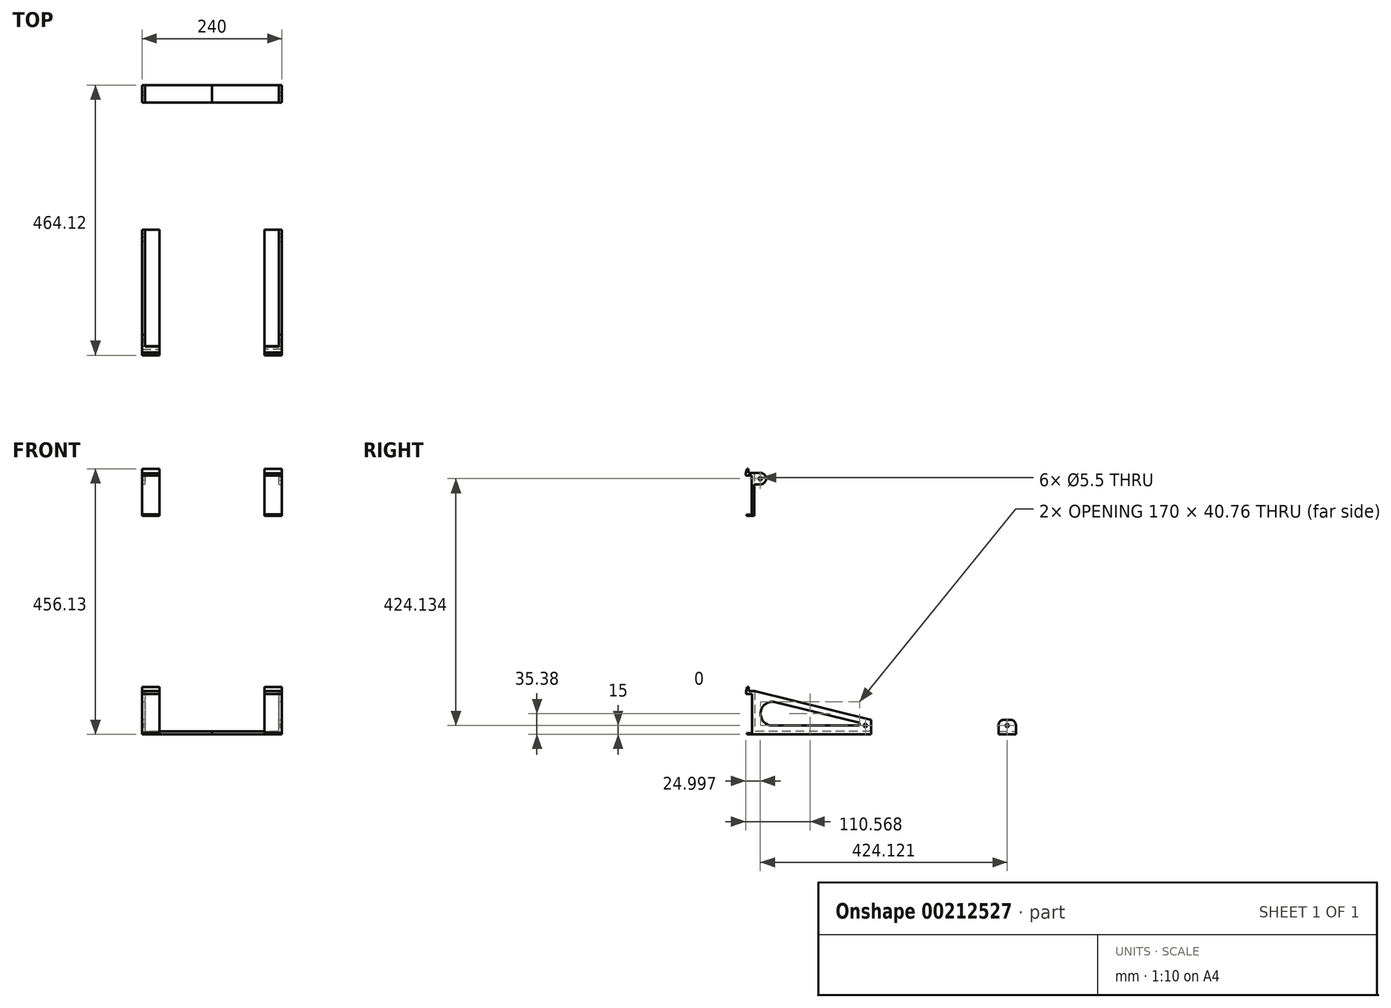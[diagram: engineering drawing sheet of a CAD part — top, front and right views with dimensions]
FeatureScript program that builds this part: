
annotation { "Feature Type Name" : "Feature", "Feature Type Description" : "" }
export const myFeature = defineFeature(function(context is Context, id is Id, definition is map)
    precondition{}
    {
        {
            var Q0;
            Q0=qCreatedBy(makeId("Right.planeOp"),FACE);
            var sketch = newSketch(context, id + "F0", { "sketchPlane" : qUnion([Q0])});
            skLineSegment(sketch, "E0", {"start": v(2.67, -35.24) * mm, "end": v(2.67, 31.76) * mm});
            skLineSegment(sketch, "E1", {"start": v(2.67, 31.76) * mm, "end": v(-7.33, 31.76) * mm});
            skLineSegment(sketch, "E2", {"start": v(-7.33, 31.76) * mm, "end": v(-7.33, 36.87) * mm});
            skLineSegment(sketch, "E3", {"start": v(-5.08, 43.76) * mm, "end": v(-2.83, 43.76) * mm});
            skLineSegment(sketch, "E4", {"start": v(-2.83, 43.76) * mm, "end": v(-2.83, 36.76) * mm});
            skLineSegment(sketch, "E5", {"start": v(-2.83, 36.76) * mm, "end": v(7.67, 36.76) * mm});
            skLineSegment(sketch, "E6", {"start": v(7.67, 36.76) * mm, "end": v(7.67, -32.24) * mm});
            skLineSegment(sketch, "E7", {"start": v(7.67, -37.24) * mm, "end": v(-5.83, -37.24) * mm});
            skLineSegment(sketch, "E8", {"start": v(-5.83, -37.24) * mm, "end": v(-5.83, -35.24) * mm});
            skLineSegment(sketch, "E9", {"start": v(-2.83, -35.24) * mm, "end": v(2.67, -35.24) * mm});
            skLineSegment(sketch, "E10", {"start": v(-5.08, 43.76) * mm, "end": v(-7.33, 36.87) * mm});
            skPoint(sketch, "E11.orphan", {"position": v(-7.33, 43.76) * mm});
            skLineSegment(sketch, "E12", {"start": v(-2.83, -35.24) * mm, "end": v(-4.33, -34.5) * mm});
            skLineSegment(sketch, "E13", {"start": v(-4.33, -34.5) * mm, "end": v(-5.83, -35.24) * mm});
            skPoint(sketch, "E14.orphan", {"position": v(-5.83, -34.5) * mm});
            skLineSegment(sketch, "E15", {"start": v(7.67, -37.24) * mm, "end": v(207.67, -37.24) * mm});
            skLineSegment(sketch, "E16", {"start": v(207.67, -37.24) * mm, "end": v(207.67, -32.24) * mm});
            skLineSegment(sketch, "E17", {"start": v(207.67, -32.24) * mm, "end": v(7.67, -32.24) * mm});
            skSolve(sketch);
        }
        {
            var Q0;
            Q0=makeQuery(id+"F0.imprint","IMPRINT",FACE,{"disambiguationData":[TD([[makeQuery(id+"F0.imprint","IMPRINT",EDGE,{"derivedFrom":sQuery(id+"F0.wireOp",EDGE,"E0")}),-1.0]])]});
            extrude(context, id + "F1", {"entities" : qUnion([Q0]), "depth" : 30 * mm});
        }
        {
            var Q0;
            Q0=makeQuery(id+"F1.opExtrude","CAP_FACE",FACE,{"disambiguationData":[OSD([sQuery(id+"F0.wireOp",EDGE,"E0"),sQuery(id+"F0.wireOp",EDGE,"E1"),sQuery(id+"F0.wireOp",EDGE,"E2"),sQuery(id+"F0.wireOp",EDGE,"E3"),sQuery(id+"F0.wireOp",EDGE,"E4"),sQuery(id+"F0.wireOp",EDGE,"E5"),sQuery(id+"F0.wireOp",EDGE,"E6"),sQuery(id+"F0.wireOp",EDGE,"E7"),sQuery(id+"F0.wireOp",EDGE,"E8"),sQuery(id+"F0.wireOp",EDGE,"E9"),sQuery(id+"F0.wireOp",EDGE,"E10"),sQuery(id+"F0.wireOp",EDGE,"E12"),sQuery(id+"F0.wireOp",EDGE,"E13"),sQuery(id+"F0.wireOp",EDGE,"E15"),sQuery(id+"F0.wireOp",EDGE,"E16"),sQuery(id+"F0.wireOp",EDGE,"E17")])],"isStart":false});
            var sketch = newSketch(context, id + "F2", { "sketchPlane" : qUnion([Q0])});
            skLineSegment(sketch, "E18", {"start": v(7.67, 36.76) * mm, "end": v(7.67, -32.24) * mm});
            skLineSegment(sketch, "E19", {"start": v(7.67, -32.24) * mm, "end": v(207.67, -32.24) * mm});
            skLineSegment(sketch, "E20", {"start": v(207.67, -32.24) * mm, "end": v(207.67, -12.24) * mm});
            skLineSegment(sketch, "E21", {"start": v(207.67, -12.24) * mm, "end": v(7.67, 36.76) * mm});
            skLineSegment(sketch, "E22", {"start": v(207.67, -22.24) * mm, "end": v(197.67, -22.24) * mm, "construction": true});
            skPoint(sketch, "E22.endSnap0", {"position": v(207.67, -22.24) * mm});
            skCircle(sketch, "E23", {"center": v(197.67, -22.24) * mm, "radius": 2.75 * mm});
            skLineSegment(sketch, "E24", {"start": v(207.67, -32.24) * mm, "end": v(187.67, -32.24) * mm, "construction": true});
            skLineSegment(sketch, "E25", {"start": v(187.67, -32.24) * mm, "end": v(187.67, -22.24) * mm, "construction": true});
            skLineSegment(sketch, "E26", {"start": v(187.67, -22.24) * mm, "end": v(17.67, -22.24) * mm});
            skLineSegment(sketch, "E27", {"start": v(187.67, -22.24) * mm, "end": v(187.67, -17.64) * mm});
            skLineSegment(sketch, "E28.trimOffspring", {"start": v(17.67, 24.01) * mm, "end": v(17.67, -22.24) * mm});
            skLineSegment(sketch, "E29.trimOffspring", {"start": v(187.67, -17.64) * mm, "end": v(17.67, 24.01) * mm});
            skSolve(sketch);
        }
        {
            var Q0;
            Q0=makeQuery(id+"F2.imprint","IMPRINT",FACE,{"disambiguationData":[TD([[makeQuery(id+"F2.imprint","IMPRINT",EDGE,{"derivedFrom":sQuery(id+"F2.wireOp",EDGE,"E18")}),1.0]])]});
            extrude(context, id + "F3", {"entities" : qUnion([Q0]), "operationType" : NewBodyOperationType.ADD, "oppositeDirection" : true, "depth" : 5 * mm});
        }
        {
            var Q0;
            Q0=makeQuery(id+"F3.opExtrude","SWEPT_EDGE",EDGE,{"disambiguationData":[OSD([sQuery(id+"F2.wireOp",EDGE,"E26"),sQuery(id+"F2.wireOp",EDGE,"E28.trimOffspring")])]});
            var Q1;
            Q1=makeQuery(id+"F3.opExtrude","SWEPT_EDGE",EDGE,{"disambiguationData":[OSD([sQuery(id+"F2.wireOp",EDGE,"E28.trimOffspring"),sQuery(id+"F2.wireOp",EDGE,"E29.trimOffspring")])]});
            fillet(context, id + "F4", {"entities" : qUnion([Q0, Q1]), "radius" : 20 * mm, "tangentPropagation" : true, "allowEdgeOverflow" : false});
        }
        {
            var Q0;
            Q0=makeQuery(id+"F3.opExtrude","SWEPT_EDGE",EDGE,{"disambiguationData":[OSD([sQuery(id+"F2.wireOp",EDGE,"E26"),sQuery(id+"F2.wireOp",EDGE,"E27")])]});
            var Q1;
            Q1=makeQuery(id+"F3.opExtrude","SWEPT_EDGE",EDGE,{"disambiguationData":[OSD([sQuery(id+"F2.wireOp",EDGE,"E27"),sQuery(id+"F2.wireOp",EDGE,"E29.trimOffspring")])]});
            fillet(context, id + "F5", {"entities" : qUnion([Q0, Q1]), "radius" : 2 * mm, "tangentPropagation" : true, "allowEdgeOverflow" : false});
        }
        {
            var Q0;
            Q0=qCreatedBy(makeId("Right.planeOp"),FACE);
            var sketch = newSketch(context, id + "F6", { "sketchPlane" : qUnion([Q0])});
            skLineSegment(sketch, "E30", {"start": v(0, 0) * mm, "end": v(0, 375) * mm, "construction": true});
            skLineSegment(sketch, "E31", {"start": v(2.1, 339.9) * mm, "end": v(2.1, 406.9) * mm});
            skLineSegment(sketch, "E32", {"start": v(2.1, 406.9) * mm, "end": v(-7.9, 406.9) * mm});
            skLineSegment(sketch, "E33", {"start": v(-7.9, 406.9) * mm, "end": v(-7.9, 411.32) * mm});
            skLineSegment(sketch, "E34", {"start": v(-5.65, 418.9) * mm, "end": v(-3.4, 418.9) * mm});
            skLineSegment(sketch, "E35", {"start": v(-3.4, 418.9) * mm, "end": v(-3.4, 411.9) * mm});
            skLineSegment(sketch, "E36", {"start": v(-3.4, 411.9) * mm, "end": v(7.1, 411.9) * mm});
            skLineSegment(sketch, "E37", {"start": v(7.1, 411.9) * mm, "end": v(7.1, 337.9) * mm});
            skLineSegment(sketch, "E38", {"start": v(7.1, 337.9) * mm, "end": v(-6.4, 337.9) * mm});
            skLineSegment(sketch, "E39", {"start": v(-6.4, 337.9) * mm, "end": v(-6.4, 339.9) * mm});
            skLineSegment(sketch, "E40", {"start": v(-3.4, 339.9) * mm, "end": v(2.1, 339.9) * mm});
            skLineSegment(sketch, "E41", {"start": v(-5.65, 418.9) * mm, "end": v(-7.9, 411.32) * mm});
            skPoint(sketch, "E42.orphan", {"position": v(-7.9, 418.9) * mm});
            skLineSegment(sketch, "E43", {"start": v(-3.4, 339.9) * mm, "end": v(-4.9, 340.64) * mm});
            skLineSegment(sketch, "E44", {"start": v(-4.9, 340.64) * mm, "end": v(-6.4, 339.9) * mm});
            skSolve(sketch);
        }
        {
            var Q0;
            Q0=makeQuery(id+"F6.imprint","IMPRINT",FACE,{"disambiguationData":[TD([[makeQuery(id+"F6.imprint","IMPRINT",EDGE,{"derivedFrom":sQuery(id+"F6.wireOp",EDGE,"E31")}),-1.0]])]});
            extrude(context, id + "F7", {"entities" : qUnion([Q0]), "depth" : 30 * mm});
        }
        {
            var Q0;
            Q0=makeQuery(id+"F7.opExtrude","CAP_FACE",FACE,{"disambiguationData":[OSD([sQuery(id+"F6.wireOp",EDGE,"E31"),sQuery(id+"F6.wireOp",EDGE,"E32"),sQuery(id+"F6.wireOp",EDGE,"E33"),sQuery(id+"F6.wireOp",EDGE,"E34"),sQuery(id+"F6.wireOp",EDGE,"E35"),sQuery(id+"F6.wireOp",EDGE,"E36"),sQuery(id+"F6.wireOp",EDGE,"E37"),sQuery(id+"F6.wireOp",EDGE,"E38"),sQuery(id+"F6.wireOp",EDGE,"E39"),sQuery(id+"F6.wireOp",EDGE,"E40"),sQuery(id+"F6.wireOp",EDGE,"E41"),sQuery(id+"F6.wireOp",EDGE,"E43"),sQuery(id+"F6.wireOp",EDGE,"E44")])],"isStart":false});
            var sketch = newSketch(context, id + "F8", { "sketchPlane" : qUnion([Q0])});
            skLineSegment(sketch, "E45", {"start": v(7.1, 411.9) * mm, "end": v(27.1, 411.9) * mm});
            skLineSegment(sketch, "E46", {"start": v(27.1, 411.9) * mm, "end": v(27.1, 391.9) * mm});
            skLineSegment(sketch, "E47", {"start": v(27.1, 391.9) * mm, "end": v(7.1, 391.9) * mm});
            skLineSegment(sketch, "E48", {"start": v(7.1, 391.9) * mm, "end": v(7.1, 411.9) * mm});
            skLineSegment(sketch, "E49", {"start": v(27.1, 401.9) * mm, "end": v(17.1, 401.9) * mm, "construction": true});
            skCircle(sketch, "E50", {"center": v(17.1, 401.9) * mm, "radius": 2.75 * mm});
            skSolve(sketch);
        }
        {
            var Q0;
            Q0=makeQuery(id+"F8.imprint","IMPRINT",FACE,{"disambiguationData":[TD([[makeQuery(id+"F8.imprint","IMPRINT",EDGE,{"derivedFrom":sQuery(id+"F8.wireOp",EDGE,"E45")}),-1.0]])]});
            extrude(context, id + "F9", {"entities" : qUnion([Q0]), "operationType" : NewBodyOperationType.ADD, "oppositeDirection" : true, "depth" : 5 * mm});
        }
        {
            var Q0;
            Q0=makeQuery(id+"F9.opExtrude","SWEPT_EDGE",EDGE,{"disambiguationData":[OSD([sQuery(id+"F8.wireOp",EDGE,"E45"),sQuery(id+"F8.wireOp",EDGE,"E46")])]});
            var Q1;
            Q1=makeQuery(id+"F9.opExtrude","SWEPT_EDGE",EDGE,{"disambiguationData":[OSD([sQuery(id+"F8.wireOp",EDGE,"E46"),sQuery(id+"F8.wireOp",EDGE,"E47")])]});
            var Q2;
            Q2=makeQuery(id+"F9.opExtrude","SWEPT_EDGE",EDGE,{"disambiguationData":[OSD([sQuery(id+"F6.wireOp",EDGE,"E37"),sQuery(id+"F8.wireOp",EDGE,"E47"),sQuery(id+"F8.wireOp",EDGE,"E48")])]});
            fillet(context, id + "F10", {"entities" : qUnion([Q0, Q1, Q2]), "radius" : 10 * mm, "tangentPropagation" : true, "allowEdgeOverflow" : false});
        }
        {
            var Q0;
            Q0=makeQuery(id+"F9.boolean.opBoolean","MERGE",FACE,{"derivedFrom":[makeQuery(id+"F7.opExtrude","CAP_FACE",FACE,{"disambiguationData":[OSD([sQuery(id+"F6.wireOp",EDGE,"E31"),sQuery(id+"F6.wireOp",EDGE,"E32"),sQuery(id+"F6.wireOp",EDGE,"E33"),sQuery(id+"F6.wireOp",EDGE,"E34"),sQuery(id+"F6.wireOp",EDGE,"E35"),sQuery(id+"F6.wireOp",EDGE,"E36"),sQuery(id+"F6.wireOp",EDGE,"E37"),sQuery(id+"F6.wireOp",EDGE,"E38"),sQuery(id+"F6.wireOp",EDGE,"E39"),sQuery(id+"F6.wireOp",EDGE,"E40"),sQuery(id+"F6.wireOp",EDGE,"E41"),sQuery(id+"F6.wireOp",EDGE,"E43"),sQuery(id+"F6.wireOp",EDGE,"E44")])],"isStart":false}),makeQuery(id+"F9.opExtrude","CAP_FACE",FACE,{"disambiguationData":[OSD([sQuery(id+"F8.wireOp",EDGE,"E45"),sQuery(id+"F8.wireOp",EDGE,"E46"),sQuery(id+"F8.wireOp",EDGE,"E47"),sQuery(id+"F8.wireOp",EDGE,"E48"),sQuery(id+"F8.wireOp",EDGE,"E50")])],"isStart":true})]});
            var sketch = newSketch(context, id + "F11", { "sketchPlane" : qUnion([Q0])});
            skLineSegment(sketch, "E51", {"start": v(17.1, 401.9) * mm, "end": v(782.83, -363.84) * mm, "construction": true});
            skLineSegment(sketch, "E52", {"start": v(17.1, 401.9) * mm, "end": v(17.1, -201.82) * mm, "construction": true});
            skLineSegment(sketch, "E53", {"start": v(197.74, -22.23) * mm, "end": v(609.04, -22.23) * mm, "construction": true});
            skCircle(sketch, "E54", {"center": v(441.22, -22.23) * mm, "radius": 2.75 * mm});
            skLineSegment(sketch, "E55", {"start": v(441.22, -22.23) * mm, "end": v(441.22, -37.23) * mm, "construction": true});
            skLineSegment(sketch, "E56", {"start": v(441.22, -37.23) * mm, "end": v(426.22, -37.23) * mm});
            skLineSegment(sketch, "E57", {"start": v(426.22, -37.23) * mm, "end": v(426.22, -12.23) * mm});
            skLineSegment(sketch, "E58", {"start": v(426.22, -12.23) * mm, "end": v(456.22, -12.23) * mm});
            skLineSegment(sketch, "E59", {"start": v(456.22, -12.23) * mm, "end": v(456.22, -37.23) * mm});
            skLineSegment(sketch, "E60", {"start": v(456.22, -37.23) * mm, "end": v(441.22, -37.23) * mm});
            skSolve(sketch);
        }
        {
            var Q0;
            Q0=makeQuery(id+"F11.imprint","IMPRINT",FACE,{"disambiguationData":[TD([[makeQuery(id+"F11.imprint","IMPRINT",EDGE,{"derivedFrom":sQuery(id+"F11.wireOp",EDGE,"E54")}),-1.0]])]});
            extrude(context, id + "F12", {"entities" : qUnion([Q0]), "oppositeDirection" : true, "depth" : 5 * mm});
        }
        {
            var Q0;
            Q0=makeQuery(id+"F12.opExtrude","SWEPT_EDGE",EDGE,{"disambiguationData":[OSD([sQuery(id+"F11.wireOp",EDGE,"E57"),sQuery(id+"F11.wireOp",EDGE,"E58")])]});
            var Q1;
            Q1=makeQuery(id+"F12.opExtrude","SWEPT_EDGE",EDGE,{"disambiguationData":[OSD([sQuery(id+"F11.wireOp",EDGE,"E58"),sQuery(id+"F11.wireOp",EDGE,"E59")])]});
            fillet(context, id + "F13", {"entities" : qUnion([Q0, Q1]), "radius" : 10 * mm, "tangentPropagation" : true, "allowEdgeOverflow" : false});
        }
        {
            var Q0;
            Q0=makeQuery(id+"F12.opExtrude","SWEPT_FACE",FACE,{"disambiguationData":[OSD([sQuery(id+"F11.wireOp",EDGE,"E59")])]});
            var sketch = newSketch(context, id + "F14", { "sketchPlane" : qUnion([Q0])});
            skLineSegment(sketch, "E61", {"start": v(-25, -37.23) * mm, "end": v(90, -37.23) * mm});
            skLineSegment(sketch, "E62", {"start": v(90, -37.23) * mm, "end": v(90, -32.23) * mm});
            skLineSegment(sketch, "E63", {"start": v(90, -32.23) * mm, "end": v(-25, -32.23) * mm});
            skLineSegment(sketch, "E64", {"start": v(-25, -32.23) * mm, "end": v(-25, -37.23) * mm});
            skSolve(sketch);
        }
        {
            var Q0;
            Q0=makeQuery(id+"F14.imprint","IMPRINT",FACE,{"disambiguationData":[TD([[makeQuery(id+"F14.imprint","IMPRINT",EDGE,{"derivedFrom":sQuery(id+"F14.wireOp",EDGE,"E61")}),1.0]])]});
            extrude(context, id + "F15", {"entities" : qUnion([Q0]), "operationType" : NewBodyOperationType.ADD, "oppositeDirection" : true, "depth" : 30 * mm});
        }
        {
            var Q0;
            Q0=qCreatedBy(makeId("Right.planeOp"),FACE);
            cPlane(context, id + "F16", {"entities" : qUnion([Q0]), "cplaneType" : CPlaneType.OFFSET, "offset" : 90 * mm, "oppositeDirection" : true, "width" : 150 * mm, "height" : 150 * mm});
        }
        {
            var Q0;
            Q0=makeQuery(id+"F12.opExtrude","SWEPT_BODY",BODY,{"disambiguationData":[OSD([sQuery(id+"F11.wireOp",EDGE,"E54"),sQuery(id+"F11.wireOp",EDGE,"E56"),sQuery(id+"F11.wireOp",EDGE,"E57"),sQuery(id+"F11.wireOp",EDGE,"E58"),sQuery(id+"F11.wireOp",EDGE,"E59"),sQuery(id+"F11.wireOp",EDGE,"E60")])]});
            var Q1;
            Q1=qCreatedBy(id+"F16.planeOp",FACE);
            mirror(context, id + "F17", {"operationType" : NewBodyOperationType.ADD, "entities" : qUnion([Q0]), "mirrorPlane" : qUnion([Q1])});
        }
        {
            var Q0;
            Q0=makeQuery(id+"F1.opExtrude","SWEPT_BODY",BODY,{"disambiguationData":[OSD([sQuery(id+"F0.wireOp",EDGE,"E0"),sQuery(id+"F0.wireOp",EDGE,"E1"),sQuery(id+"F0.wireOp",EDGE,"E2"),sQuery(id+"F0.wireOp",EDGE,"E3"),sQuery(id+"F0.wireOp",EDGE,"E4"),sQuery(id+"F0.wireOp",EDGE,"E5"),sQuery(id+"F0.wireOp",EDGE,"E6"),sQuery(id+"F0.wireOp",EDGE,"E7"),sQuery(id+"F0.wireOp",EDGE,"E8"),sQuery(id+"F0.wireOp",EDGE,"E9"),sQuery(id+"F0.wireOp",EDGE,"E10"),sQuery(id+"F0.wireOp",EDGE,"E12"),sQuery(id+"F0.wireOp",EDGE,"E13"),sQuery(id+"F0.wireOp",EDGE,"E15"),sQuery(id+"F0.wireOp",EDGE,"E16"),sQuery(id+"F0.wireOp",EDGE,"E17")])]});
            var Q1;
            Q1=makeQuery(id+"F7.opExtrude","SWEPT_BODY",BODY,{"disambiguationData":[OSD([sQuery(id+"F6.wireOp",EDGE,"E31"),sQuery(id+"F6.wireOp",EDGE,"E32"),sQuery(id+"F6.wireOp",EDGE,"E33"),sQuery(id+"F6.wireOp",EDGE,"E34"),sQuery(id+"F6.wireOp",EDGE,"E35"),sQuery(id+"F6.wireOp",EDGE,"E36"),sQuery(id+"F6.wireOp",EDGE,"E37"),sQuery(id+"F6.wireOp",EDGE,"E38"),sQuery(id+"F6.wireOp",EDGE,"E39"),sQuery(id+"F6.wireOp",EDGE,"E40"),sQuery(id+"F6.wireOp",EDGE,"E41"),sQuery(id+"F6.wireOp",EDGE,"E43"),sQuery(id+"F6.wireOp",EDGE,"E44")])]});
            var Q2;
            Q2=qCreatedBy(id+"F16.planeOp",FACE);
            mirror(context, id + "F18", {"entities" : qUnion([Q0, Q1]), "mirrorPlane" : qUnion([Q2])});
        }
    });
